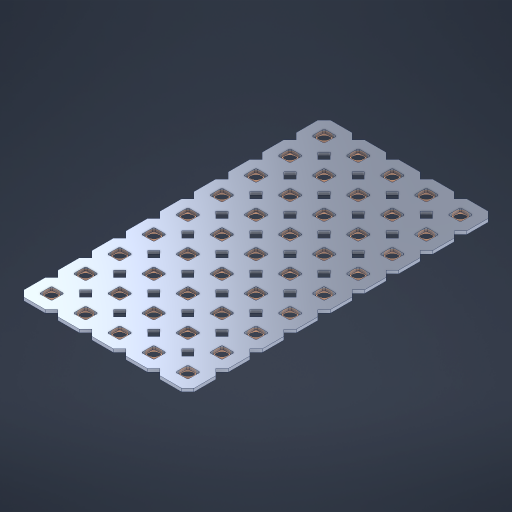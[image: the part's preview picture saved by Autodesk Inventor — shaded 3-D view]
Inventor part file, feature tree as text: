
AUTODESK INVENTOR PART (.ipt)
format: ipt  version: 2023 (Build 270158000, 158)  size: 785,920 bytes
history: native  units: in
note: dims shown in document units (in); Inventor stores cm internally (conversion verified against a paired STEP export)
features: other x46, extrude x44, sketch x2, pattern_linear x1
ambient origin geometry x8: Origin, YZ Plane, XZ Plane, XY Plane, X Axis, Y Axis, Z Axis, Center Point
bodies: Solid1 (feature_tree), Body (feature_tree)
feature tree (93):
  pattern_linear  "Rectangular Pattern1"  Spacing1=0.09in  [1 undecoded]
  sketch  "Sketch1"  dims[d1=0.5in]
  sketch  "Sketch2"  dims[d2=0.182in d3=0.09in d4=0.09in d5=0.09in d6=0.09in d7=0.09in d8=0.09in d9=0.09in d10=0.09in d11=0.02in d13=0.0in d14=0.172in d15=0.0625in d16=0.0in d19=0.5in d22=0.5in]
  other  "Srf1"
  other  "Srf126"
  other  "Srf127"
  other  "Srf128"
  other  "Srf129"
  other  "Srf130"
  other  "Srf131"
  other  "Srf250"
  other  "Srf251"
  other  "Srf268"
  other  "Srf269"
  other  "Srf270"
  other  "Srf271"
  other  "Srf272"
  other  "Srf273"
  other  "Srf274"
  other  "Srf275"
  other  "Srf276"
  other  "Srf293"
  other  "Srf294"
  other  "Srf295"
  other  "Srf296"
  other  "Srf297"
  other  "Srf298"
  other  "Srf299"
  other  "Srf300"
  other  "Srf301"
  other  "Srf318"
  other  "Srf319"
  other  "Srf320"
  other  "Srf321"
  other  "Srf322"
  other  "Srf323"
  other  "Srf324"
  other  "Srf325"
  other  "Srf326"
  other  "Srf343"
  other  "Srf344"
  other  "Srf345"
  other  "Srf346"
  other  "Srf347"
  other  "Srf348"
  other  "Srf349"
  other  "Srf350"
  other  "Srf351"
  other  "Circle"
  extrude  "ExtrusionSrf126"  Depth=0.09in
  extrude  "ExtrusionSrf127"  Depth=0.09in
  extrude  "ExtrusionSrf128"  Depth=0.09in
  extrude  "ExtrusionSrf129"  Depth=0.09in
  extrude  "ExtrusionSrf130"  Depth=0.09in
  extrude  "ExtrusionSrf131"  Depth=0.09in
  extrude  "ExtrusionSrf250"  Depth=0.09in
  extrude  "ExtrusionSrf251"  Depth=0.02in
  extrude  "ExtrusionSrf268"  TaperAngle=0.0deg  [1 undecoded]
  extrude  "ExtrusionSrf269"  Depth=0.5in
  extrude  "ExtrusionSrf270"  Depth=0.5in TaperAngle=0.0deg
  extrude  "ExtrusionSrf271"  Depth=0.5in
  extrude  "ExtrusionSrf272"  Depth=0.5in
  extrude  "ExtrusionSrf273"  [1 undecoded]
  extrude  "ExtrusionSrf274"  [1 undecoded]
  extrude  "ExtrusionSrf275"  [1 undecoded]
  extrude  "ExtrusionSrf276"  [1 undecoded]
  extrude  "ExtrusionSrf293"  [1 undecoded]
  extrude  "ExtrusionSrf294"  [1 undecoded]
  extrude  "ExtrusionSrf295"  [1 undecoded]
  extrude  "ExtrusionSrf296"  [1 undecoded]
  extrude  "ExtrusionSrf297"  [1 undecoded]
  extrude  "ExtrusionSrf298"  [1 undecoded]
  extrude  "ExtrusionSrf299"  [1 undecoded]
  extrude  "ExtrusionSrf300"  [1 undecoded]
  extrude  "ExtrusionSrf301"  [1 undecoded]
  extrude  "ExtrusionSrf318"  [1 undecoded]
  extrude  "ExtrusionSrf319"  [1 undecoded]
  extrude  "ExtrusionSrf320"  [1 undecoded]
  extrude  "ExtrusionSrf321"  [1 undecoded]
  extrude  "ExtrusionSrf322"  [1 undecoded]
  extrude  "ExtrusionSrf323"  [1 undecoded]
  extrude  "ExtrusionSrf324"  [1 undecoded]
  extrude  "ExtrusionSrf325"  [1 undecoded]
  extrude  "ExtrusionSrf326"  [1 undecoded]
  extrude  "ExtrusionSrf343"  [1 undecoded]
  extrude  "ExtrusionSrf344"  [1 undecoded]
  extrude  "ExtrusionSrf345"  [1 undecoded]
  extrude  "ExtrusionSrf346"  [1 undecoded]
  extrude  "ExtrusionSrf347"  [1 undecoded]
  extrude  "ExtrusionSrf348"  [1 undecoded]
  extrude  "ExtrusionSrf349"  [1 undecoded]
  extrude  "ExtrusionSrf350"  [1 undecoded]
  extrude  "ExtrusionSrf351"  [1 undecoded]
note: 33 required parameter values undecoded (feature->parameter linkage not recoverable at this tier; creation-order binding heuristic only, values carry confidence <= 0.55)
